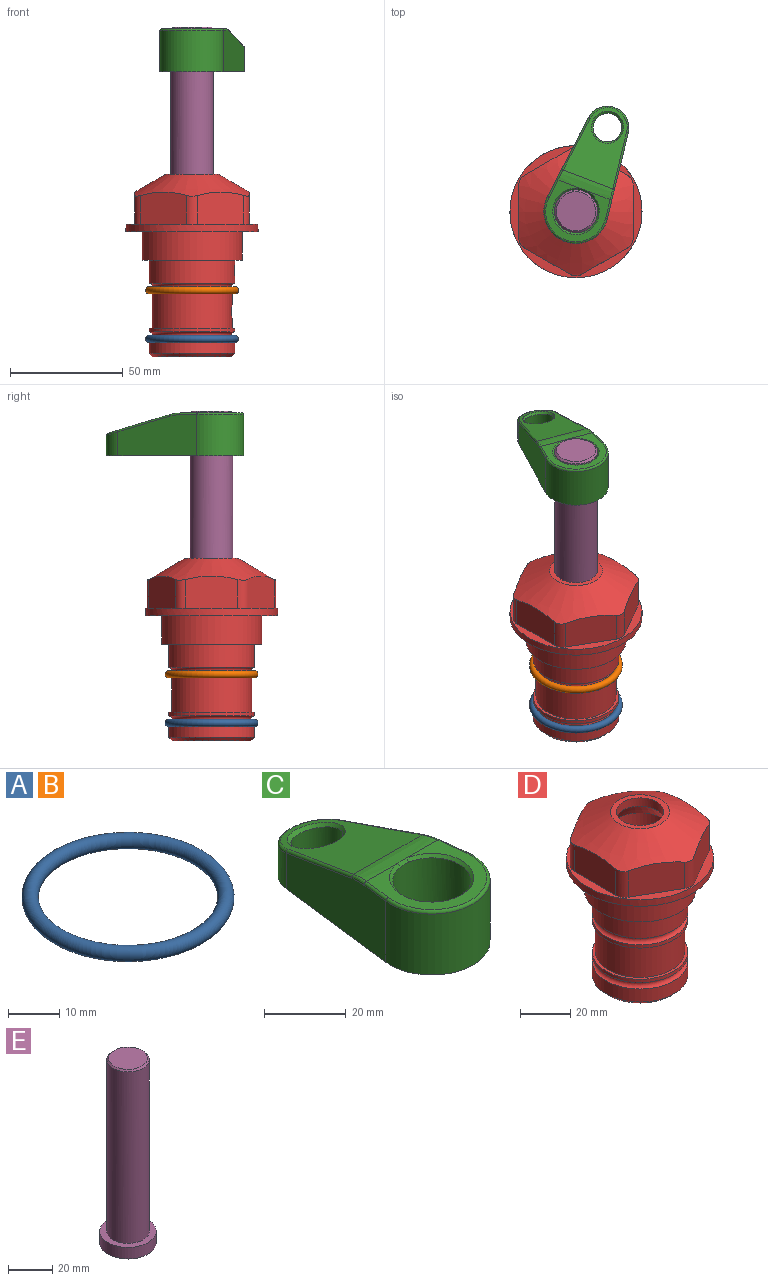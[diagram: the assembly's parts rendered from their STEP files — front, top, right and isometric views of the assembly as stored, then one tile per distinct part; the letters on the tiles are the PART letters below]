
ASSEMBLY  parts=5 mates=4
PART A: 1 faces, bbox 44.7x44.7x3.2 mm
  f0: torus R=19.05mm, axis (0,0,1), area 1193.9mm2
PART B: same geometry as A
PART C: 31 faces, bbox 31.7x65.5x19.8 mm
  f0: plane 39.12x18.26mm, normal (0.99,0.12,0), area 612.2mm2, adj f1,f4,f7,f11,f13,f15
  f1: cylinder r=9.53mm len=18.91mm, axis (0,0,-1), area 296.1mm2, adj f0,f2,f7,f17
  f2: plane 39.12x18.26mm, normal (-0.99,0.12,0), area 612.2mm2, adj f1,f4,f7,f12,f14,f16
  f3: cylinder r=6.35mm len=12.7mm, axis (0,0,-1), area 362.4mm2, adj f7,f18
  f4: cylinder r=14.29mm len=28.58mm, axis (0,0,-1), area 882.2mm2, adj f0,f2,f7,f10
  f5: cylinder r=9.53mm len=19.05mm, axis (0,0,-1), area 1092.6mm2, adj f7,f19,f20
  f6: plane 26.99x23.69mm, normal (0,0,1), area 216.2mm2, adj f9,f10,f11,f12,f19
  f7: plane 63.5x28.58mm, normal (0,0,-1), area 661.8mm2, adj f0,f1,f2,f3,f4,f5,f22,f23
  f8: plane 33.52x23.6mm, normal (0,0.26,0.97), area 486mm2, adj f9,f15,f16,f17,f18
  f9: cylinder r=19.05mm len=24.72mm, axis (1,0,0), area 120.4mm2, adj f6,f8,f13,f14,f20
  f10: torus R=13.49mm, axis (0,0,1), area 59mm2, adj f4,f6,f11,f12
  f11: cylinder r=0.79mm len=8.67mm, axis (0.12,-0.99,0), area 10.8mm2, adj f0,f6,f10,f13
  f12: cylinder r=0.79mm len=8.67mm, axis (0.12,0.99,0), area 10.8mm2, adj f2,f6,f10,f14
  f13: bspline ~4.95x1.42mm, area 6.1mm2, adj f0,f9,f11,f15
  f14: bspline ~4.95x1.42mm, area 6.1mm2, adj f2,f9,f12,f16
  f15: cylinder r=0.79mm len=25.95mm, axis (0.12,-0.96,0.26), area 32.9mm2, adj f0,f8,f13,f17
  f16: cylinder r=0.79mm len=25.95mm, axis (0.12,0.96,-0.26), area 32.9mm2, adj f2,f8,f14,f17
  f17: bspline ~18.91x8.38mm, area 30mm2, adj f1,f8,f15,f16
  f18: bspline ~14.29x14.29mm, area 48.3mm2, adj f3,f8
  f19: cone r=9.53mm half-angle=45deg, axis (0,0,1), area 66.5mm2, adj f5,f6,f20
  f20: bspline ~3.22x0.96mm, area 3.5mm2, adj f5,f9,f19
  f21: plane 2.75x2.72mm, normal (0,0,-1), area 2.9mm2, adj f23,f25,f28
  f22: plane 23.05x15.88mm, normal (-0.99,-0.12,0), area 323.6mm2, adj f7,f25,f26,f27,f28,f29
  f23: plane 23.05x15.88mm, normal (0.99,-0.12,0), area 323.6mm2, adj f7,f21,f25,f27,f28,f30
  f24: cylinder r=9.53mm len=10.69mm, axis (0,0,-1), area 114.7mm2, adj f7,f27,f29,f30
  f25: cylinder r=12.7mm len=20.59mm, axis (0,0,-1), area 381.1mm2, adj f7,f21,f22,f23,f26,f28
  f26: plane 2.75x2.72mm, normal (0,0,-1), area 2.9mm2, adj f22,f25,f28
  f27: plane 19.72x18.37mm, normal (0,-0.26,-0.97), area 291.8mm2, adj f22,f23,f24,f28,f29,f30
  f28: cylinder r=15.88mm len=19.92mm, axis (1,0,0), area 54.8mm2, adj f21,f22,f23,f25,f26,f27
  f29: cylinder r=1.59mm len=11mm, axis (0,0,-1), area 34.7mm2, adj f7,f22,f24,f27
  f30: cylinder r=1.59mm len=11mm, axis (0,0,-1), area 34.7mm2, adj f7,f23,f24,f27
PART D: 36 faces, bbox 58.7x58.7x81 mm
  f0: cylinder r=17.78mm len=35.56mm, axis (0,0,1), area 1670.8mm2, adj f23,f24,f31
  f1: cylinder r=19.05mm len=38.1mm, axis (0,0,1), area 1191.9mm2, adj f26,f27,f30
  f2: plane 58.66x58.66mm, normal (0,0,-1), area 1150.6mm2, adj f3,f28
  f3: cylinder r=29.33mm len=58.66mm, axis (0,0,-1), area 585.1mm2, adj f2,f4
  f4: plane 58.66x58.66mm, normal (0,0,1), area 475.9mm2, adj f3,f5,f6,f7,f8,f9,f10,f11
  f5: plane 20.32x14.34mm, normal (-0.5,0.87,0), area 324.4mm2, adj f4,f15,f16,f17
  f6: plane 20.32x14.34mm, normal (0.5,0.87,0), area 324.4mm2, adj f4,f14,f15,f17
  f7: plane 23.48x14.34mm, normal (1,0,0), area 324.4mm2, adj f4,f13,f14,f17
  f8: plane 20.32x14.34mm, normal (0.5,-0.87,0), area 324.4mm2, adj f4,f12,f13,f17
  f9: plane 20.32x14.34mm, normal (-0.5,-0.87,0), area 324.4mm2, adj f4,f11,f12,f17
  f10: plane 23.48x14.34mm, normal (-1,0,0), area 324.4mm2, adj f4,f11,f16,f17
  f11: cylinder r=5.08mm len=12.85mm, axis (0,0,-1), area 67.2mm2, adj f4,f9,f10,f17
  f12: cylinder r=5.08mm len=12.85mm, axis (0,0,-1), area 67.2mm2, adj f4,f8,f9,f17
  f13: cylinder r=5.08mm len=12.85mm, axis (0,0,-1), area 67.2mm2, adj f4,f7,f8,f17
  f14: cylinder r=5.08mm len=12.85mm, axis (0,0,-1), area 67.2mm2, adj f4,f6,f7,f17
  f15: cylinder r=5.08mm len=12.85mm, axis (0,0,-1), area 67.2mm2, adj f4,f5,f6,f17
  f16: cylinder r=5.08mm len=12.85mm, axis (0,0,-1), area 67.2mm2, adj f4,f5,f10,f17
  f17: cone r=11.73mm half-angle=60deg, axis (0,0,-1), area 2071.8mm2, adj f5,f6,f7,f8,f9,f10,f11,f12
  f18: plane 23.46x23.46mm, normal (0,0,1), area 147.4mm2, adj f17,f35
  f19: plane 34.93x34.93mm, normal (0,0,-1), area 958mm2, adj f29
  f20: cylinder r=19.05mm len=38.1mm, axis (0,0,1), area 760.1mm2, adj f21,f29
  f21: torus R=19.05mm, axis (0,0,1), area 565.3mm2, adj f20,f22
  f22: cylinder r=19.05mm len=38.1mm, axis (0,0,1), area 190mm2, adj f21,f23
  f23: plane 38.1x38.1mm, normal (0,0,1), area 146.9mm2, adj f0,f22
  f24: plane 38.1x38.1mm, normal (0,0,-1), area 146.9mm2, adj f0,f25
  f25: cylinder r=19.05mm len=38.1mm, axis (0,0,1), area 190mm2, adj f24,f26
  f26: torus R=19.05mm, axis (0,0,1), area 565.3mm2, adj f1,f25
  f27: plane 44.45x44.45mm, normal (0,0,-1), area 411.7mm2, adj f1,f28
  f28: cylinder r=22.23mm len=44.45mm, axis (0,0,1), area 1773.5mm2, adj f2,f27
  f29: cone r=19.05mm half-angle=45deg, axis (0,0,1), area 257.5mm2, adj f19,f20
  f30: cylinder r=3.17mm len=6.75mm, axis (-1,0,0), area 128mm2, adj f1,f33
  f31: cylinder r=3.17mm len=6.35mm, axis (-1,0,0), area 102.5mm2, adj f0,f33
  f32: plane 25.4x25.4mm, normal (0,0,1), area 506.7mm2, adj f33
  f33: cylinder r=12.7mm len=66.42mm, axis (0,0,-1), area 5236.2mm2, adj f30,f31,f32,f34
  f34: cone r=9.53mm half-angle=30deg, axis (0,0,-1), area 443.4mm2, adj f33,f35
  f35: cylinder r=9.53mm len=19.05mm, axis (0,0,-1), area 240.9mm2, adj f18,f34
PART E: 6 faces, bbox 25.4x25.4x101.6 mm
  f0: plane 17.46x17.46mm, normal (0,0,1), area 239.5mm2, adj f5
  f1: plane 25.4x25.4mm, normal (0,0,-1), area 506.7mm2, adj f2
  f2: cylinder r=12.7mm len=25.4mm, axis (0,0,1), area 506.7mm2, adj f1,f3
  f3: plane 25.4x25.4mm, normal (0,0,1), area 221.7mm2, adj f2,f4
  f4: cylinder r=9.53mm len=94.46mm, axis (0,0,1), area 5653mm2, adj f3,f5
  f5: cone r=8.73mm half-angle=45deg, axis (0,0,-1), area 64.4mm2, adj f0,f4
PLACE A t=(0,0,-23.18)mm
PLACE B t=(0,0,-1.59)mm
PLACE C rot(axis=(0,0,-1),20.6deg) t=(0,0,26.44)mm
PLACE D at identity fixed
PLACE E rot(axis=(0,0,-1),20.6deg) t=(0,0,27.24)mm
MATE fastened B.f0 <-> D.f0  axis (0,0,1) through (0,0,-26.1)mm
MATE fastened A.f0 <-> D.f0  axis (0,0,1) through (0,0,-47.69)mm
MATE cylindrical E.f2 <-> D.f0  axis (0,0,-1) through (0,0,-10.86)mm
MATE fastened C.f4 <-> E.f2  axis (0,0,1) through (0,0,89.94)mm
